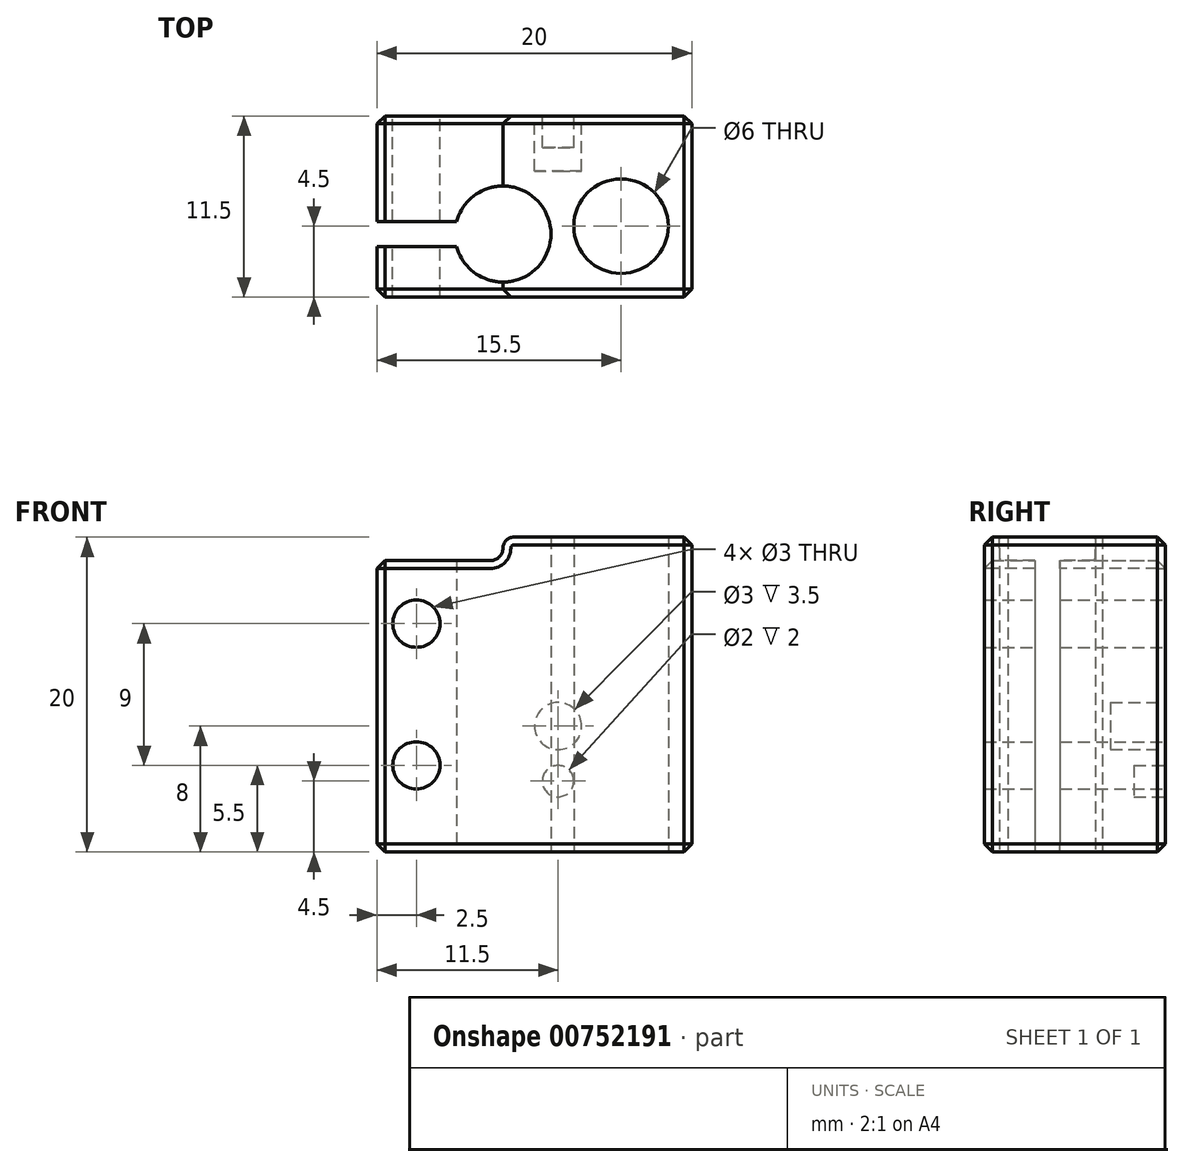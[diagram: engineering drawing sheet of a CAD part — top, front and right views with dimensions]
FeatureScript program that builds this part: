
annotation { "Feature Type Name" : "Feature", "Feature Type Description" : "" }
export const myFeature = defineFeature(function(context is Context, id is Id, definition is map)
    precondition{}
    {
        {
            var Q0;
            Q0=qCreatedBy(makeId("Front.planeOp"),FACE);
            var sketch = newSketch(context, id + "F0", { "sketchPlane" : qUnion([Q0])});
            skLineSegment(sketch, "E0.bottom", {"start": v(4.5, -20) * mm, "end": v(-6.8, -20) * mm});
            skLineSegment(sketch, "E0.top", {"start": v(4.5, 0) * mm, "end": v(-15.5, 0) * mm});
            skLineSegment(sketch, "E0.left", {"start": v(4.5, -20) * mm, "end": v(4.5, 0) * mm});
            skLineSegment(sketch, "E0.right", {"start": v(-15.5, -18.5) * mm, "end": v(-15.5, 0) * mm});
            skLineSegment(sketch, "E1", {"start": v(-15.5, -18.5) * mm, "end": v(-8.3, -18.5) * mm});
            skLineSegment(sketch, "E2", {"start": v(-7.5, 0.7) * mm, "end": v(-7.5, 0.7) * mm});
            skPoint(sketch, "E3", {"position": v(-13, -14.5) * mm});
            skPoint(sketch, "E4", {"position": v(-13, -5.5) * mm});
            skPoint(sketch, "E5", {"position": v(-4, -4.5) * mm});
            skPoint(sketch, "E6", {"position": v(-4, -8) * mm});
            skPoint(sketch, "E7.visualSharp", {"position": v(-7.5, -18.5) * mm});
            skArc(sketch, "E7.filletArc", {"start": v(-7.5, -19.3) * mm, "mid": v(-7.73, -18.73) * mm, "end": v(-8.3, -18.5) * mm});
            skLineSegment(sketch, "E8", {"start": v(0, -47.98) * mm, "end": v(0, 21.9) * mm, "construction": true});
            skPoint(sketch, "E9", {"position": v(0, -20) * mm});
            skCircle(sketch, "E10", {"center": v(-4, -8) * mm, "radius": 1.2 * mm});
            skCircle(sketch, "E11", {"center": v(-4, -8) * mm, "radius": 1.5 * mm});
            skCircle(sketch, "E12", {"center": v(-4, -4.5) * mm, "radius": 1 * mm});
            skPoint(sketch, "E13.visualSharp", {"position": v(-7.5, -20) * mm});
            skArc(sketch, "E13.filletArc", {"start": v(-7.5, -19.3) * mm, "mid": v(-7.3, -19.8) * mm, "end": v(-6.8, -20) * mm});
            skCircle(sketch, "E14", {"center": v(-13, -5.5) * mm, "radius": 1.2 * mm});
            skCircle(sketch, "E15", {"center": v(-13, -5.5) * mm, "radius": 1.5 * mm});
            skCircle(sketch, "E16", {"center": v(-13, -14.5) * mm, "radius": 1.2 * mm});
            skCircle(sketch, "E17", {"center": v(-13, -14.5) * mm, "radius": 1.5 * mm});
            skPoint(sketch, "E18", {"position": v(0, 0) * mm});
            skPoint(sketch, "E19", {"position": v(159.93, -108.2) * mm});
            skSolve(sketch);
        }
        {
            var Q0;
            Q0=makeQuery(id+"F0.imprint","IMPRINT",FACE,{"disambiguationData":[TD([[makeQuery(id+"F0.imprint","IMPRINT",EDGE,{"derivedFrom":sQuery(id+"F0.wireOp",EDGE,"E0.bottom")}),-1.0]])]});
            var Q1;
            Q1=makeQuery(id+"F0.imprint","IMPRINT",FACE,{"disambiguationData":[TD([[makeQuery(id+"F0.imprint","IMPRINT",EDGE,{"derivedFrom":sQuery(id+"F0.wireOp",EDGE,"E10")}),1.0]])]});
            var Q2;
            Q2=makeQuery(id+"F0.imprint","IMPRINT",FACE,{"disambiguationData":[TD([[makeQuery(id+"F0.imprint","IMPRINT",EDGE,{"derivedFrom":sQuery(id+"F0.wireOp",EDGE,"E10")}),-1.0]])]});
            var Q3;
            Q3=makeQuery(id+"F0.imprint","IMPRINT",FACE,{"disambiguationData":[TD([[makeQuery(id+"F0.imprint","IMPRINT",EDGE,{"derivedFrom":sQuery(id+"F0.wireOp",EDGE,"E12")}),1.0]])]});
            var Q4;
            Q4=makeQuery(id+"F0.imprint","IMPRINT",FACE,{"disambiguationData":[TD([[makeQuery(id+"F0.imprint","IMPRINT",EDGE,{"derivedFrom":sQuery(id+"F0.wireOp",EDGE,"E14")}),-1.0]])]});
            var Q5;
            Q5=makeQuery(id+"F0.imprint","IMPRINT",FACE,{"disambiguationData":[TD([[makeQuery(id+"F0.imprint","IMPRINT",EDGE,{"derivedFrom":sQuery(id+"F0.wireOp",EDGE,"E14")}),1.0]])]});
            var Q6;
            Q6=makeQuery(id+"F0.imprint","IMPRINT",FACE,{"disambiguationData":[TD([[makeQuery(id+"F0.imprint","IMPRINT",EDGE,{"derivedFrom":sQuery(id+"F0.wireOp",EDGE,"E16")}),-1.0]])]});
            var Q7;
            Q7=makeQuery(id+"F0.imprint","IMPRINT",FACE,{"disambiguationData":[TD([[makeQuery(id+"F0.imprint","IMPRINT",EDGE,{"derivedFrom":sQuery(id+"F0.wireOp",EDGE,"E16")}),1.0]])]});
            extrude(context, id + "F1", {"entities" : qUnion([Q0, Q1, Q2, Q3, Q4, Q5, Q6, Q7]), "depth" : 11.5 * mm, "offsetDistance" : 25 * mm});
        }
        {
            var Q0;
            Q0=qCreatedBy(makeId("Top.planeOp"),FACE);
            var sketch = newSketch(context, id + "F2", { "sketchPlane" : qUnion([Q0])});
            skLineSegment(sketch, "E20.bottom", {"start": v(-15.5, 0) * mm, "end": v(4.5, 0) * mm});
            skLineSegment(sketch, "E20.top", {"start": v(-15.5, -11.5) * mm, "end": v(4.5, -11.5) * mm});
            skLineSegment(sketch, "E20.left", {"start": v(-15.5, 0) * mm, "end": v(-15.5, -6.7) * mm});
            skLineSegment(sketch, "E20.right", {"start": v(4.5, 0) * mm, "end": v(4.5, -11.5) * mm});
            skLineSegment(sketch, "E21.0", {"start": v(-15.5, 4.8) * mm, "end": v(-15.5, -11.5) * mm, "construction": true});
            skLineSegment(sketch, "E22.0", {"start": v(4.5, 0) * mm, "end": v(-15.5, 0) * mm, "construction": true});
            skLineSegment(sketch, "E23.0", {"start": v(4.5, 0) * mm, "end": v(4.5, -11.5) * mm, "construction": true});
            skLineSegment(sketch, "E24.0", {"start": v(-15.5, -11.5) * mm, "end": v(4.5, -11.5) * mm, "construction": true});
            skPoint(sketch, "E25", {"position": v(-15.5, -11.5) * mm});
            skPoint(sketch, "E26", {"position": v(-7.5, -7.5) * mm});
            skPoint(sketch, "E27", {"position": v(0, -7) * mm});
            skPoint(sketch, "E28", {"position": v(-15.5, -8.3) * mm});
            skPoint(sketch, "E29", {"position": v(-15.5, -6.7) * mm});
            skArc(sketch, "E30", {"start": v(-10.44, -8.3) * mm, "mid": v(-4.45, -7.5) * mm, "end": v(-10.44, -6.7) * mm});
            skCircle(sketch, "E31", {"center": v(0, -7) * mm, "radius": 2.4 * mm});
            skCircle(sketch, "E32", {"center": v(0, -7) * mm, "radius": 3 * mm});
            skLineSegment(sketch, "E33", {"start": v(-15.5, -6.7) * mm, "end": v(-10.44, -6.7) * mm});
            skLineSegment(sketch, "E34", {"start": v(-15.5, -8.3) * mm, "end": v(-10.44, -8.3) * mm});
            skLineSegment(sketch, "E35.trimOffspring", {"start": v(-15.5, -8.3) * mm, "end": v(-15.5, -11.5) * mm, "construction": true});
            skLineSegment(sketch, "E36.trimOffspring", {"start": v(-15.5, -8.3) * mm, "end": v(-15.5, -11.5) * mm});
            skLineSegment(sketch, "E37", {"start": v(-15.5, -8.3) * mm, "end": v(-15.5, -6.7) * mm});
            skSolve(sketch);
        }
        {
            var Q0;
            Q0=makeQuery(id+"F2.imprint","IMPRINT",FACE,{"disambiguationData":[TD([[makeQuery(id+"F2.imprint","IMPRINT",EDGE,{"derivedFrom":sQuery(id+"F2.wireOp",EDGE,"E30")}),1.0]])]});
            var Q1;
            Q1=makeQuery(id+"F2.imprint","IMPRINT",FACE,{"disambiguationData":[TD([[makeQuery(id+"F2.imprint","IMPRINT",EDGE,{"derivedFrom":sQuery(id+"F2.wireOp",EDGE,"E31")}),1.0]])]});
            var Q2;
            Q2=makeQuery(id+"F2.imprint","IMPRINT",FACE,{"disambiguationData":[TD([[makeQuery(id+"F2.imprint","IMPRINT",EDGE,{"derivedFrom":sQuery(id+"F2.wireOp",EDGE,"E31")}),-1.0]])]});
            extrude(context, id + "F3", {"entities" : qUnion([Q0, Q1, Q2]), "operationType" : NewBodyOperationType.REMOVE, "oppositeDirection" : true, "depth" : 25 * mm, "offsetDistance" : 25 * mm});
        }
        {
            var Q0;
            Q0=makeQuery(id+"F0.imprint","IMPRINT",FACE,{"disambiguationData":[TD([[makeQuery(id+"F0.imprint","IMPRINT",EDGE,{"derivedFrom":sQuery(id+"F0.wireOp",EDGE,"E14")}),1.0]])]});
            var Q1;
            Q1=makeQuery(id+"F0.imprint","IMPRINT",FACE,{"disambiguationData":[TD([[makeQuery(id+"F0.imprint","IMPRINT",EDGE,{"derivedFrom":sQuery(id+"F0.wireOp",EDGE,"E16")}),1.0]])]});
            var Q2;
            Q2=makeQuery(id+"F0.imprint","IMPRINT",FACE,{"disambiguationData":[TD([[makeQuery(id+"F0.imprint","IMPRINT",EDGE,{"derivedFrom":sQuery(id+"F0.wireOp",EDGE,"E14")}),-1.0]])]});
            var Q3;
            Q3=makeQuery(id+"F0.imprint","IMPRINT",FACE,{"disambiguationData":[TD([[makeQuery(id+"F0.imprint","IMPRINT",EDGE,{"derivedFrom":sQuery(id+"F0.wireOp",EDGE,"E16")}),-1.0]])]});
            extrude(context, id + "F4", {"entities" : qUnion([Q0, Q1, Q2, Q3]), "operationType" : NewBodyOperationType.REMOVE, "depth" : 25 * mm, "offsetDistance" : 25 * mm});
        }
        {
            var Q0;
            Q0=makeQuery(id+"F0.imprint","IMPRINT",FACE,{"disambiguationData":[TD([[makeQuery(id+"F0.imprint","IMPRINT",EDGE,{"derivedFrom":sQuery(id+"F0.wireOp",EDGE,"E10")}),-1.0]])]});
            var Q1;
            Q1=makeQuery(id+"F0.imprint","IMPRINT",FACE,{"disambiguationData":[TD([[makeQuery(id+"F0.imprint","IMPRINT",EDGE,{"derivedFrom":sQuery(id+"F0.wireOp",EDGE,"E10")}),1.0]])]});
            extrude(context, id + "F5", {"entities" : qUnion([Q0, Q1]), "operationType" : NewBodyOperationType.REMOVE, "depth" : 3.5 * mm, "offsetDistance" : 25 * mm});
        }
        {
            var Q0;
            Q0=makeQuery(id+"F0.imprint","IMPRINT",FACE,{"disambiguationData":[TD([[makeQuery(id+"F0.imprint","IMPRINT",EDGE,{"derivedFrom":sQuery(id+"F0.wireOp",EDGE,"E12")}),1.0]])]});
            extrude(context, id + "F6", {"entities" : qUnion([Q0]), "operationType" : NewBodyOperationType.REMOVE, "depth" : 2 * mm, "offsetDistance" : 25 * mm});
        }
        {
            var Q0;
            Q0=makeQuery(id+"F1.opExtrude","SWEPT_EDGE",EDGE,{"disambiguationData":[OSD([sQuery(id+"F0.wireOp",EDGE,"E0.top"),sQuery(id+"F0.wireOp",EDGE,"E0.left")])]});
            var Q1;
            Q1=makeQuery(id+"F1.opExtrude","CAP_EDGE",EDGE,{"disambiguationData":[OSD([sQuery(id+"F0.wireOp",EDGE,"E0.top")])],"isStart":false});
            var Q2;
            {var subQ0=sQuery(id+"F0.wireOp",EDGE,"E0.right");var subQ1=sQuery(id+"F0.wireOp",EDGE,"E0.top");Q2=makeQuery(id+"F3.boolean.opBoolean","SPLIT",EDGE,{"disambiguationData":[TD([makeQuery(id+"F3.opExtrude","SWEPT_FACE",FACE,{"disambiguationData":[OSD([sQuery(id+"F2.wireOp",EDGE,"E34")])]})])],"derivedFrom":makeQuery(id+"F1.opExtrude","SWEPT_EDGE",EDGE,{"disambiguationData":[OSD([subQ1,subQ0])]})});}
            var Q3;
            {var subQ0=sQuery(id+"F0.wireOp",EDGE,"E0.right");var subQ1=sQuery(id+"F0.wireOp",EDGE,"E0.top");Q3=makeQuery(id+"F3.boolean.opBoolean","SPLIT",EDGE,{"disambiguationData":[TD([makeQuery(id+"F3.opExtrude","SWEPT_FACE",FACE,{"disambiguationData":[OSD([sQuery(id+"F2.wireOp",EDGE,"E33")])]})])],"derivedFrom":makeQuery(id+"F1.opExtrude","SWEPT_EDGE",EDGE,{"disambiguationData":[OSD([subQ1,subQ0])]})});}
            var Q4;
            Q4=makeQuery(id+"F1.opExtrude","CAP_EDGE",EDGE,{"disambiguationData":[OSD([sQuery(id+"F0.wireOp",EDGE,"E0.top")])],"isStart":true});
            var Q5;
            Q5=makeQuery(id+"F1.opExtrude","CAP_EDGE",EDGE,{"disambiguationData":[OSD([sQuery(id+"F0.wireOp",EDGE,"E0.left")])],"isStart":false});
            var Q6;
            Q6=makeQuery(id+"F1.opExtrude","CAP_EDGE",EDGE,{"disambiguationData":[OSD([sQuery(id+"F0.wireOp",EDGE,"E0.right")])],"isStart":false});
            var Q7;
            Q7=makeQuery(id+"F1.opExtrude","CAP_EDGE",EDGE,{"disambiguationData":[OSD([sQuery(id+"F0.wireOp",EDGE,"E1")])],"isStart":false});
            var Q8;
            Q8=makeQuery(id+"F1.opExtrude","CAP_EDGE",EDGE,{"disambiguationData":[OSD([sQuery(id+"F0.wireOp",EDGE,"E7.filletArc")])],"isStart":false});
            var Q9;
            Q9=makeQuery(id+"F1.opExtrude","CAP_EDGE",EDGE,{"disambiguationData":[OSD([sQuery(id+"F0.wireOp",EDGE,"E13.filletArc")])],"isStart":false});
            var Q10;
            Q10=makeQuery(id+"F1.opExtrude","CAP_EDGE",EDGE,{"disambiguationData":[OSD([sQuery(id+"F0.wireOp",EDGE,"E0.bottom")])],"isStart":false});
            var Q11;
            Q11=makeQuery(id+"F1.opExtrude","SWEPT_EDGE",EDGE,{"disambiguationData":[OSD([sQuery(id+"F0.wireOp",EDGE,"E0.bottom"),sQuery(id+"F0.wireOp",EDGE,"E0.left")])]});
            var Q12;
            {var subQ0=sQuery(id+"F0.wireOp",EDGE,"E1");var subQ1=sQuery(id+"F0.wireOp",EDGE,"E0.right");Q12=makeQuery(id+"F3.boolean.opBoolean","SPLIT",EDGE,{"disambiguationData":[TD([makeQuery(id+"F3.opExtrude","SWEPT_FACE",FACE,{"disambiguationData":[OSD([sQuery(id+"F2.wireOp",EDGE,"E34")])]})])],"derivedFrom":makeQuery(id+"F1.opExtrude","SWEPT_EDGE",EDGE,{"disambiguationData":[OSD([subQ1,subQ0])]})});}
            var Q13;
            {var subQ0=sQuery(id+"F0.wireOp",EDGE,"E1");var subQ1=sQuery(id+"F0.wireOp",EDGE,"E0.right");Q13=makeQuery(id+"F3.boolean.opBoolean","SPLIT",EDGE,{"disambiguationData":[TD([makeQuery(id+"F3.opExtrude","SWEPT_FACE",FACE,{"disambiguationData":[OSD([sQuery(id+"F2.wireOp",EDGE,"E33")])]})])],"derivedFrom":makeQuery(id+"F1.opExtrude","SWEPT_EDGE",EDGE,{"disambiguationData":[OSD([subQ1,subQ0])]})});}
            var Q14;
            Q14=makeQuery(id+"F1.opExtrude","CAP_EDGE",EDGE,{"disambiguationData":[OSD([sQuery(id+"F0.wireOp",EDGE,"E0.left")])],"isStart":true});
            var Q15;
            Q15=makeQuery(id+"F1.opExtrude","CAP_EDGE",EDGE,{"disambiguationData":[OSD([sQuery(id+"F0.wireOp",EDGE,"E0.bottom")])],"isStart":true});
            var Q16;
            Q16=makeQuery(id+"F1.opExtrude","CAP_EDGE",EDGE,{"disambiguationData":[OSD([sQuery(id+"F0.wireOp",EDGE,"E13.filletArc")])],"isStart":true});
            var Q17;
            Q17=makeQuery(id+"F1.opExtrude","CAP_EDGE",EDGE,{"disambiguationData":[OSD([sQuery(id+"F0.wireOp",EDGE,"E7.filletArc")])],"isStart":true});
            var Q18;
            Q18=makeQuery(id+"F1.opExtrude","CAP_EDGE",EDGE,{"disambiguationData":[OSD([sQuery(id+"F0.wireOp",EDGE,"E1")])],"isStart":true});
            var Q19;
            Q19=makeQuery(id+"F1.opExtrude","CAP_EDGE",EDGE,{"disambiguationData":[OSD([sQuery(id+"F0.wireOp",EDGE,"E0.right")])],"isStart":true});
            chamfer(context, id + "F7", {"entities" : qUnion([Q0, Q1, Q2, Q3, Q4, Q5, Q6, Q7, Q8, Q9, Q10, Q11, Q12, Q13, Q14, Q15, Q16, Q17, Q18, Q19]), "width" : 0.5 * mm, "tangentPropagation" : true});
        }
        {
            var Q0;
            Q0=makeQuery(id+"F1.opExtrude","SWEPT_BODY",BODY,{"disambiguationData":[OSD([sQuery(id+"F0.wireOp",EDGE,"E0.bottom"),sQuery(id+"F0.wireOp",EDGE,"E0.top"),sQuery(id+"F0.wireOp",EDGE,"E0.left"),sQuery(id+"F0.wireOp",EDGE,"E0.right"),sQuery(id+"F0.wireOp",EDGE,"E1"),sQuery(id+"F0.wireOp",EDGE,"E7.filletArc"),sQuery(id+"F0.wireOp",EDGE,"E13.filletArc")])]});
            var Q1;
            Q1=qCreatedBy(makeId("Front.planeOp"),FACE);
            mirror(context, id + "F8", {"entities" : qUnion([Q0]), "mirrorPlane" : qUnion([Q1])});
        }
        {
            var Q0;
            Q0=makeQuery(id+"F1.opExtrude","SWEPT_BODY",BODY,{"disambiguationData":[OSD([sQuery(id+"F0.wireOp",EDGE,"E0.bottom"),sQuery(id+"F0.wireOp",EDGE,"E0.top"),sQuery(id+"F0.wireOp",EDGE,"E0.left"),sQuery(id+"F0.wireOp",EDGE,"E0.right"),sQuery(id+"F0.wireOp",EDGE,"E1"),sQuery(id+"F0.wireOp",EDGE,"E7.filletArc"),sQuery(id+"F0.wireOp",EDGE,"E13.filletArc")])]});
            deleteBodies(context, id + "F9", {"entities" : qUnion([Q0])});
        }
        {
            var Q0;
            Q0=makeQuery(id+"F8.opPattern","COPY",BODY,{"derivedFrom":makeQuery(id+"F1.opExtrude","SWEPT_BODY",BODY,{"disambiguationData":[OSD([sQuery(id+"F0.wireOp",EDGE,"E0.bottom"),sQuery(id+"F0.wireOp",EDGE,"E0.top"),sQuery(id+"F0.wireOp",EDGE,"E0.left"),sQuery(id+"F0.wireOp",EDGE,"E0.right"),sQuery(id+"F0.wireOp",EDGE,"E1"),sQuery(id+"F0.wireOp",EDGE,"E7.filletArc"),sQuery(id+"F0.wireOp",EDGE,"E13.filletArc")])]}),"instanceName":"1"});
            var Q1;
            {var subQ0=sQuery(id+"F0.wireOp",EDGE,"E0.top");Q1=makeQuery(id+"F8.opPattern","COPY",EDGE,{"derivedFrom":makeQuery(id+"F7.opChamfer","BLEND_EDGE",EDGE,{"blendedFrom":[makeQuery(id+"F1.opExtrude","CAP_EDGE",EDGE,{"disambiguationData":[OSD([subQ0])],"isStart":true}),makeQuery(id+"F1.opExtrude","CAP_FACE",FACE,{"disambiguationData":[OSD([sQuery(id+"F0.wireOp",EDGE,"E0.bottom"),subQ0,sQuery(id+"F0.wireOp",EDGE,"E0.left"),sQuery(id+"F0.wireOp",EDGE,"E0.right"),sQuery(id+"F0.wireOp",EDGE,"E1"),sQuery(id+"F0.wireOp",EDGE,"E7.filletArc"),sQuery(id+"F0.wireOp",EDGE,"E13.filletArc")])],"isStart":true})],"blendedInto":[makeQuery(id+"F1.opExtrude","CAP_FACE",FACE,{"disambiguationData":[OSD([sQuery(id+"F0.wireOp",EDGE,"E0.bottom"),subQ0,sQuery(id+"F0.wireOp",EDGE,"E0.left"),sQuery(id+"F0.wireOp",EDGE,"E0.right"),sQuery(id+"F0.wireOp",EDGE,"E1"),sQuery(id+"F0.wireOp",EDGE,"E7.filletArc"),sQuery(id+"F0.wireOp",EDGE,"E13.filletArc")])],"isStart":true})]}),"instanceName":"1"});}
            transform(context, id + "F10", {"entities" : qUnion([Q0]), "transformType" : TransformType.ROTATION, "transformAxis" : qUnion([Q1]), "angle" : 180 * degree, "makeCopy" : false});
        }
    });
